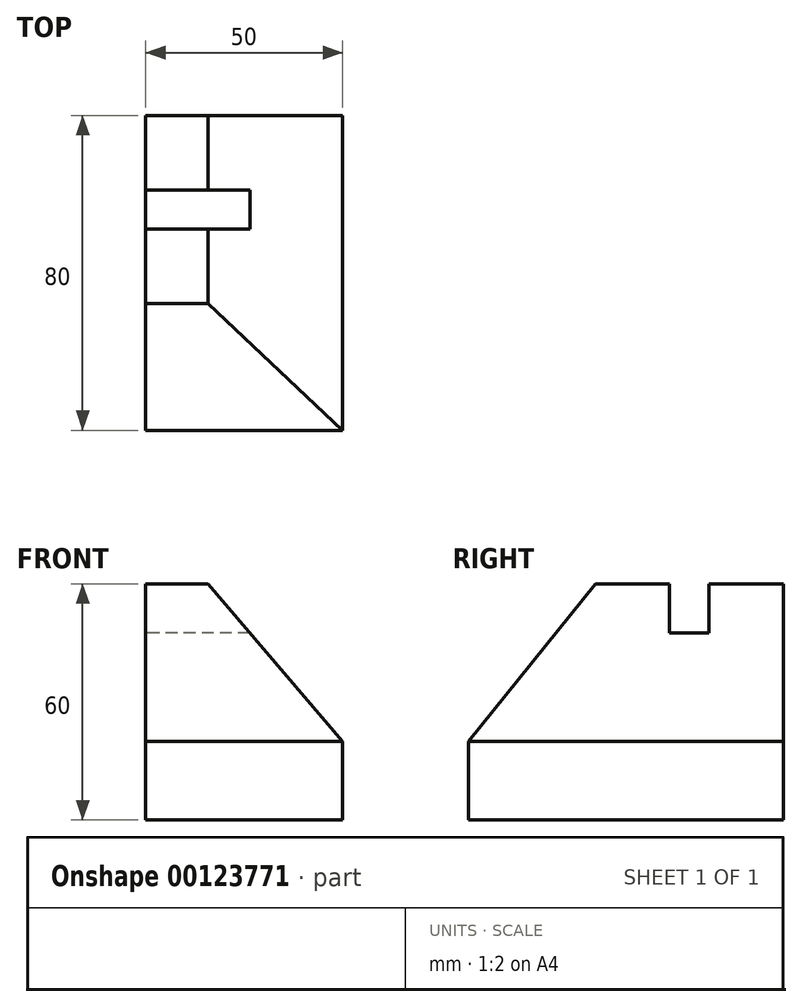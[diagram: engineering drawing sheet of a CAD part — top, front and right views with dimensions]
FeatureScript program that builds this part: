
annotation { "Feature Type Name" : "Feature", "Feature Type Description" : "" }
export const myFeature = defineFeature(function(context is Context, id is Id, definition is map)
    precondition{}
    {
        {
            var Q0;
            Q0=qCreatedBy(makeId("Top.planeOp"),FACE);
            var sketch = newSketch(context, id + "F0", { "sketchPlane" : qUnion([Q0])});
            skLineSegment(sketch, "E0", {"start": v(0, 0) * mm, "end": v(50, 0) * mm});
            skLineSegment(sketch, "E1", {"start": v(50, 0) * mm, "end": v(50, 80) * mm});
            skLineSegment(sketch, "E2", {"start": v(50, 80) * mm, "end": v(0, 80) * mm});
            skLineSegment(sketch, "E3", {"start": v(0, 80) * mm, "end": v(0, 0) * mm});
            skSolve(sketch);
        }
        {
            var Q0;
            Q0=makeQuery(id+"F0.imprint","IMPRINT",FACE,{"disambiguationData":[TD([[makeQuery(id+"F0.imprint","IMPRINT",EDGE,{"derivedFrom":sQuery(id+"F0.wireOp",EDGE,"E0")}),1.0]])]});
            extrude(context, id + "F1", {"entities" : qUnion([Q0]), "depth" : 60 * mm});
        }
        {
            var Q0;
            Q0=makeQuery(id+"F1.opExtrude","SWEPT_FACE",FACE,{"disambiguationData":[OSD([sQuery(id+"F0.wireOp",EDGE,"E0")])]});
            var sketch = newSketch(context, id + "F2", { "sketchPlane" : qUnion([Q0])});
            skLineSegment(sketch, "E4", {"start": v(50, 60) * mm, "end": v(15.8, 60) * mm});
            skLineSegment(sketch, "E5", {"start": v(15.8, 60) * mm, "end": v(50, 20) * mm});
            skLineSegment(sketch, "E6", {"start": v(50, 20) * mm, "end": v(50, 60) * mm});
            skSolve(sketch);
        }
        {
            var Q0;
            Q0 = qSketchRegion(id + "F2", true);
            extrude(context, id + "F3", {"entities" : qUnion([Q0]), "operationType" : NewBodyOperationType.REMOVE, "endBound" : BoundingType.THROUGH_ALL, "oppositeDirection" : true, "depth" : 25 * mm});
        }
        {
            var Q0;
            Q0=qCreatedBy(makeId("Right.planeOp"),FACE);
            cPlane(context, id + "F4", {"entities" : qUnion([Q0]), "cplaneType" : CPlaneType.OFFSET, "offset" : 50 * mm, "width" : 150 * mm, "height" : 150 * mm});
        }
        {
            var Q0;
            Q0=qCreatedBy(id+"F4.planeOp",FACE);
            var sketch = newSketch(context, id + "F5", { "sketchPlane" : qUnion([Q0])});
            skLineSegment(sketch, "E7", {"start": v(0, 20) * mm, "end": v(36.24, 65) * mm});
            skLineSegment(sketch, "E8", {"start": v(36.24, 65) * mm, "end": v(0, 65) * mm});
            skLineSegment(sketch, "E9", {"start": v(0, 65) * mm, "end": v(0, 20) * mm});
            skSolve(sketch);
        }
        {
            var Q0;
            Q0 = qSketchRegion(id + "F5", true);
            extrude(context, id + "F6", {"entities" : qUnion([Q0]), "operationType" : NewBodyOperationType.REMOVE, "oppositeDirection" : true, "depth" : 66.16 * mm});
        }
        {
            var Q0;
            Q0=makeQuery(id+"F1.opExtrude","SWEPT_FACE",FACE,{"disambiguationData":[OSD([sQuery(id+"F0.wireOp",EDGE,"E3")])]});
            var sketch = newSketch(context, id + "F7", { "sketchPlane" : qUnion([Q0])});
            skLineSegment(sketch, "E10", {"start": v(-56.1, 60) * mm, "end": v(-56.1, 47.54) * mm});
            skLineSegment(sketch, "E11.0", {"start": v(-61.1, 60) * mm, "end": v(-61.1, 47.54) * mm});
            skLineSegment(sketch, "E12.0", {"start": v(-51.1, 60) * mm, "end": v(-51.1, 47.54) * mm});
            skLineSegment(sketch, "E13", {"start": v(-61.1, 47.54) * mm, "end": v(-51.1, 47.54) * mm});
            skLineSegment(sketch, "E14", {"start": v(-61.1, 60) * mm, "end": v(-51.1, 60) * mm});
            skSolve(sketch);
        }
        {
            var Q0;
            Q0 = qSketchRegion(id + "F7", true);
            extrude(context, id + "F8", {"entities" : qUnion([Q0]), "operationType" : NewBodyOperationType.REMOVE, "oppositeDirection" : true, "depth" : 43.58 * mm});
        }
    });
